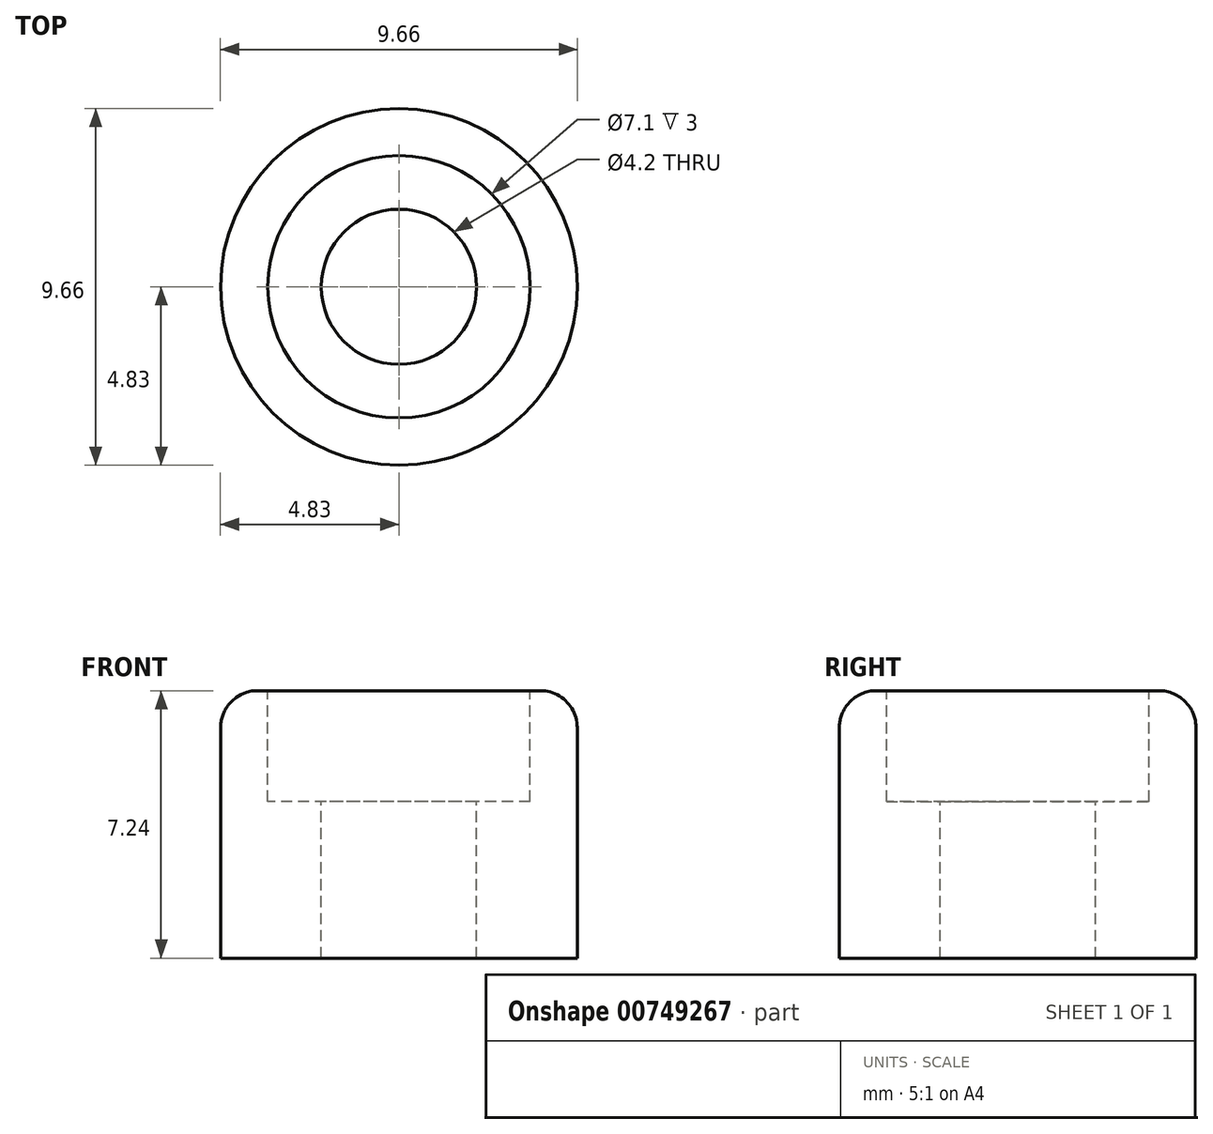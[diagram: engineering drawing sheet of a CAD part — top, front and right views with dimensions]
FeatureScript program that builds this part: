
annotation { "Feature Type Name" : "Feature", "Feature Type Description" : "" }
export const myFeature = defineFeature(function(context is Context, id is Id, definition is map)
    precondition{}
    {
        {
            var Q0;
            Q0=qCreatedBy(makeId("Top.planeOp"),FACE);
            var sketch = newSketch(context, id + "F0", { "sketchPlane" : qUnion([Q0])});
            skCircle(sketch, "E0", {"center": v(0, 0) * mm, "radius": 4.83 * mm});
            skSolve(sketch);
        }
        {
            var Q0;
            Q0=makeQuery(id+"F0.imprint","IMPRINT",FACE,{"disambiguationData":[TD([[makeQuery(id+"F0.imprint","IMPRINT",EDGE,{"derivedFrom":sQuery(id+"F0.wireOp",EDGE,"E0")}),1.0]])]});
            extrude(context, id + "F1", {"entities" : qUnion([Q0]), "oppositeDirection" : true, "depth" : 7.24 * mm, "offsetDistance" : 25 * mm});
        }
        {
            var Q0;
            Q0=makeQuery(id+"F1.opExtrude","CAP_EDGE",EDGE,{"disambiguationData":[OSD([sQuery(id+"F0.wireOp",EDGE,"E0")])],"isStart":true});
            fillet(context, id + "F2", {"entities" : qUnion([Q0]), "radius" : 1 * mm, "tangentPropagation" : true, "allowEdgeOverflow" : false});
        }
        {
            var Q0;
            Q0=makeQuery(id+"F1.opExtrude","CAP_FACE",FACE,{"disambiguationData":[OSD([sQuery(id+"F0.wireOp",EDGE,"E0")])],"isStart":true});
            var sketch = newSketch(context, id + "F3", { "sketchPlane" : qUnion([Q0])});
            skCircle(sketch, "E1", {"center": v(0, 0) * mm, "radius": 3.55 * mm});
            skSolve(sketch);
        }
        {
            var Q0;
            Q0=makeQuery(id+"F3.imprint","IMPRINT",FACE,{"disambiguationData":[TD([[makeQuery(id+"F3.imprint","IMPRINT",EDGE,{"derivedFrom":sQuery(id+"F3.wireOp",EDGE,"E1")}),1.0]])]});
            extrude(context, id + "F4", {"entities" : qUnion([Q0]), "operationType" : NewBodyOperationType.REMOVE, "oppositeDirection" : true, "depth" : 3 * mm, "offsetDistance" : 25 * mm});
        }
        {
            var Q0;
            Q0=makeQuery(id+"F4.boolean.opBoolean","COPY",FACE,{"derivedFrom":makeQuery(id+"F4.opExtrude","CAP_FACE",FACE,{"disambiguationData":[OSD([sQuery(id+"F3.wireOp",EDGE,"E1")])],"isStart":false})});
            var sketch = newSketch(context, id + "F5", { "sketchPlane" : qUnion([Q0])});
            skCircle(sketch, "E2", {"center": v(0, 0) * mm, "radius": 2.1 * mm});
            skSolve(sketch);
        }
        {
            var Q0;
            Q0=makeQuery(id+"F5.imprint","IMPRINT",FACE,{"disambiguationData":[TD([[makeQuery(id+"F5.imprint","IMPRINT",EDGE,{"derivedFrom":sQuery(id+"F5.wireOp",EDGE,"E2")}),1.0]])]});
            extrude(context, id + "F6", {"entities" : qUnion([Q0]), "operationType" : NewBodyOperationType.REMOVE, "endBound" : BoundingType.THROUGH_ALL, "oppositeDirection" : true, "depth" : 25 * mm, "offsetDistance" : 25 * mm});
        }
    });
